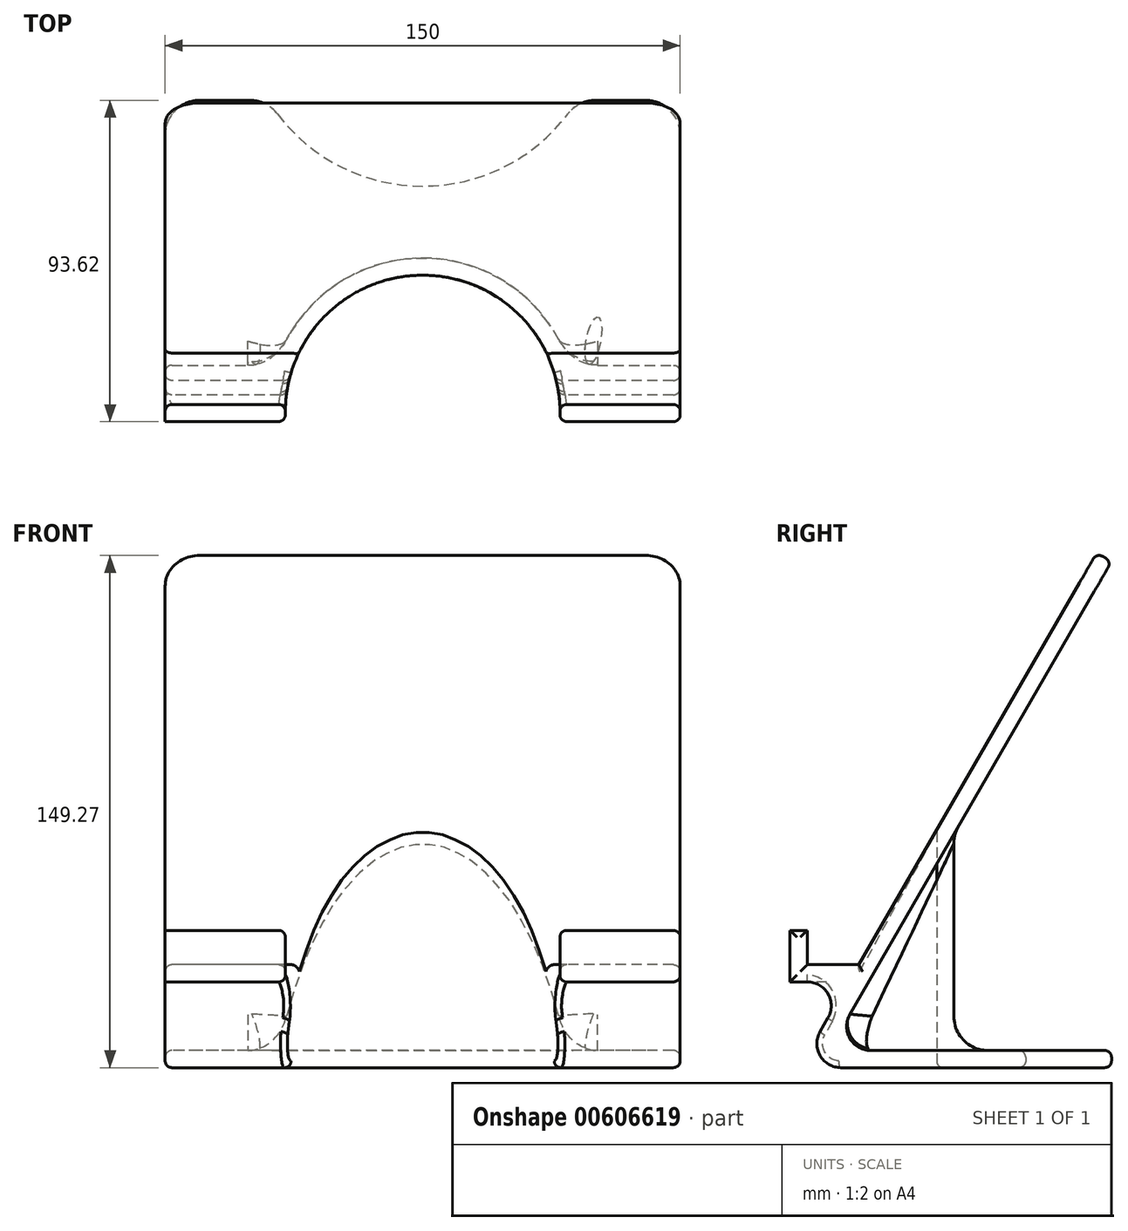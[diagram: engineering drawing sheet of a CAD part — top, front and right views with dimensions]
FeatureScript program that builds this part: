
annotation { "Feature Type Name" : "Feature", "Feature Type Description" : "" }
export const myFeature = defineFeature(function(context is Context, id is Id, definition is map)
    precondition{}
    {
        {
            var Q0;
            Q0=qCreatedBy(makeId("Right.planeOp"),FACE);
            var sketch = newSketch(context, id + "F0", { "sketchPlane" : qUnion([Q0])});
            skLineSegment(sketch, "E0", {"start": v(41.14, -35.62) * mm, "end": v(41.14, -40.62) * mm});
            skLineSegment(sketch, "E1", {"start": v(41.14, -40.62) * mm, "end": v(-49.8, -40.62) * mm});
            skLineSegment(sketch, "E2", {"start": v(-49.8, -40.62) * mm, "end": v(36.8, 109.38) * mm});
            skLineSegment(sketch, "E3", {"start": v(36.8, 109.38) * mm, "end": v(41.14, 106.88) * mm});
            skLineSegment(sketch, "E4", {"start": v(41.14, 106.88) * mm, "end": v(-41.14, -35.62) * mm});
            skLineSegment(sketch, "E5", {"start": v(-41.14, -35.63) * mm, "end": v(41.14, -35.63) * mm});
            skLineSegment(sketch, "E6", {"start": v(0, 35.63) * mm, "end": v(0, -35.63) * mm, "construction": true});
            skSolve(sketch);
        }
        {
            var Q0;
            Q0 = qSketchRegion(id + "F0", true);
            extrude(context, id + "F1", {"entities" : qUnion([Q0]), "endBound" : BoundingType.SYMMETRIC, "depth" : 150 * mm, "offsetDistance" : 25 * mm});
        }
        {
            var Q0;
            Q0=qCreatedBy(makeId("Right.planeOp"),FACE);
            var sketch = newSketch(context, id + "F2", { "sketchPlane" : qUnion([Q0])});
            skLineSegment(sketch, "E7", {"start": v(-29.59, -15.62) * mm, "end": v(-52.48, -15.62) * mm});
            skLineSegment(sketch, "E8", {"start": v(-52.48, -15.62) * mm, "end": v(-52.48, -0.62) * mm});
            skLineSegment(sketch, "E9", {"start": v(-52.48, -0.62) * mm, "end": v(-47.48, -0.62) * mm});
            skLineSegment(sketch, "E10", {"start": v(-47.48, -0.62) * mm, "end": v(-47.48, -10.62) * mm});
            skLineSegment(sketch, "E11", {"start": v(-47.48, -10.62) * mm, "end": v(-29.59, -10.62) * mm});
            skLineSegment(sketch, "E12", {"start": v(-29.59, -10.62) * mm, "end": v(-29.59, -15.62) * mm});
            skPoint(sketch, "E13", {"position": v(-32.48, -10.62) * mm});
            skSolve(sketch);
        }
        {
            var Q0;
            Q0 = qSketchRegion(id + "F2", true);
            var Q1;
            Q1=makeQuery(id+"F1.opExtrude","CAP_FACE",FACE,{"disambiguationData":[OSD([sQuery(id+"F0.wireOp",EDGE,"E0"),sQuery(id+"F0.wireOp",EDGE,"E1"),sQuery(id+"F0.wireOp",EDGE,"E2"),sQuery(id+"F0.wireOp",EDGE,"E3"),sQuery(id+"F0.wireOp",EDGE,"E4"),sQuery(id+"F0.wireOp",EDGE,"E5")])],"isStart":false});
            var Q2;
            Q2=makeQuery(id+"F1.opExtrude","CAP_FACE",FACE,{"disambiguationData":[OSD([sQuery(id+"F0.wireOp",EDGE,"E0"),sQuery(id+"F0.wireOp",EDGE,"E1"),sQuery(id+"F0.wireOp",EDGE,"E2"),sQuery(id+"F0.wireOp",EDGE,"E3"),sQuery(id+"F0.wireOp",EDGE,"E4"),sQuery(id+"F0.wireOp",EDGE,"E5")])],"isStart":true});
            extrude(context, id + "F3", {"entities" : qUnion([Q0]), "operationType" : NewBodyOperationType.ADD, "endBound" : BoundingType.UP_TO_SURFACE, "depth" : 25 * mm, "endBoundEntityFace" : qUnion([Q1]), "offsetDistance" : 25 * mm, "hasSecondDirection" : true, "secondDirectionBound" : SecondDirectionBoundingType.UP_TO_SURFACE, "secondDirectionOppositeDirection" : true, "secondDirectionDepth" : 25 * mm, "secondDirectionBoundEntityFace" : qUnion([Q2])});
        }
        {
            var Q0;
            Q0=makeQuery(id+"F1.opExtrude","SWEPT_FACE",FACE,{"disambiguationData":[OSD([sQuery(id+"F0.wireOp",EDGE,"E1")])]});
            var sketch = newSketch(context, id + "F4", { "sketchPlane" : qUnion([Q0])});
            skCircle(sketch, "E14", {"center": v(0, 49.8) * mm, "radius": 45 * mm});
            skCircle(sketch, "E15", {"center": v(0, 49.8) * mm, "radius": 40 * mm});
            skPoint(sketch, "E16", {"position": v(-45, 49.8) * mm});
            skLineSegment(sketch, "E17.0", {"start": v(75, 49.8) * mm, "end": v(-75, 49.8) * mm});
            skSolve(sketch);
        }
        {
            var Q0;
            {var subQ0=sQuery(id+"F4.wireOp",EDGE,"E17.0");var subQ1=sQuery(id+"F4.wireOp",EDGE,"E14");var subQ2=makeQuery(id+"F4.imprint","INTERSECT",VERTEX,{"disambiguationData":[OD(0.0)],"derivedFrom":[subQ1,subQ0]});Q0=makeQuery(id+"F4.imprint","IMPRINT",FACE,{"disambiguationData":[TD([[makeQuery(id+"F4.imprint","IMPRINT",EDGE,{"disambiguationData":[TD([[subQ2,1.0]])],"derivedFrom":subQ1}),1.0]])]});}
            var Q1;
            Q1=makeQuery(id+"F1.opExtrude","SWEPT_FACE",FACE,{"disambiguationData":[OSD([sQuery(id+"F0.wireOp",EDGE,"E2")])]});
            extrude(context, id + "F5", {"entities" : qUnion([Q0]), "operationType" : NewBodyOperationType.ADD, "endBound" : BoundingType.UP_TO_SURFACE, "oppositeDirection" : true, "depth" : 25 * mm, "endBoundEntityFace" : qUnion([Q1]), "offsetDistance" : 25 * mm});
        }
        {
            var Q0;
            {var subQ0=sQuery(id+"F4.wireOp",EDGE,"E17.0");var subQ1=sQuery(id+"F4.wireOp",EDGE,"E15");var subQ2=makeQuery(id+"F4.imprint","INTERSECT",VERTEX,{"disambiguationData":[OD(0.0)],"derivedFrom":[subQ1,subQ0]});Q0=makeQuery(id+"F4.imprint","IMPRINT",FACE,{"disambiguationData":[TD([[makeQuery(id+"F4.imprint","IMPRINT",EDGE,{"disambiguationData":[TD([[subQ2,1.0]])],"derivedFrom":subQ1}),1.0]])]});}
            var Q1;
            {var subQ0=sQuery(id+"F4.wireOp",EDGE,"E17.0");var subQ1=sQuery(id+"F4.wireOp",EDGE,"E15");var subQ2=makeQuery(id+"F4.imprint","INTERSECT",VERTEX,{"disambiguationData":[OD(0.0)],"derivedFrom":[subQ1,subQ0]});Q1=makeQuery(id+"F4.imprint","IMPRINT",FACE,{"disambiguationData":[TD([[makeQuery(id+"F4.imprint","IMPRINT",EDGE,{"disambiguationData":[TD([[subQ2,-1.0]])],"derivedFrom":subQ1}),1.0]])]});}
            var Q2;
            Q2=makeQuery(id+"F1.opExtrude","SWEPT_FACE",FACE,{"disambiguationData":[OSD([sQuery(id+"F0.wireOp",EDGE,"E2")])]});
            extrude(context, id + "F6", {"entities" : qUnion([Q0, Q1]), "operationType" : NewBodyOperationType.REMOVE, "endBound" : BoundingType.THROUGH_ALL, "oppositeDirection" : true, "depth" : 25 * mm, "endBoundEntityFace" : qUnion([Q2]), "offsetDistance" : 25 * mm});
        }
        {
            var Q0;
            Q0=makeQuery(id+"F1.opExtrude","SWEPT_FACE",FACE,{"disambiguationData":[OSD([sQuery(id+"F0.wireOp",EDGE,"E1")])]});
            var sketch = newSketch(context, id + "F7", { "sketchPlane" : qUnion([Q0])});
            skCircle(sketch, "E18", {"center": v(0, -69.14) * mm, "radius": 53 * mm});
            skPoint(sketch, "E19", {"position": v(-45, -41.14) * mm});
            skPoint(sketch, "E20", {"position": v(0, -16.14) * mm});
            skSolve(sketch);
        }
        {
            var Q0;
            Q0 = qSketchRegion(id + "F7", true);
            var Q1;
            {var subQ0=sQuery(id+"F0.wireOp",EDGE,"E5");var subQ5=sQuery(id+"F0.wireOp",EDGE,"E0");Q1=makeQuery(id+"F5.boolean.opBoolean","SPLIT",FACE,{"disambiguationData":[TD([makeQuery(id+"F1.opExtrude","SWEPT_FACE",FACE,{"disambiguationData":[OSD([subQ5])]})])],"derivedFrom":makeQuery(id+"F1.opExtrude","SWEPT_FACE",FACE,{"disambiguationData":[OSD([subQ0])]})});}
            extrude(context, id + "F8", {"entities" : qUnion([Q0]), "operationType" : NewBodyOperationType.REMOVE, "endBound" : BoundingType.UP_TO_SURFACE, "oppositeDirection" : true, "depth" : 33 * mm, "endBoundEntityFace" : qUnion([Q1]), "offsetDistance" : 25 * mm});
        }
        {
            var Q0;
            {var subQ0=sQuery(id+"F2.wireOp",EDGE,"E7");var subQ1=makeQuery(id+"F3.opExtrude","SWEPT_FACE",FACE,{"disambiguationData":[OSD([subQ0])]});var subQ2=sQuery(id+"F0.wireOp",EDGE,"E2");var subQ3=makeQuery(id+"F1.opExtrude","SWEPT_FACE",FACE,{"disambiguationData":[OSD([subQ2])]});Q0=makeQuery(id+"F6.boolean.opBoolean","SPLIT",EDGE,{"disambiguationData":[TD([makeQuery(id+"F1.opExtrude","CAP_FACE",FACE,{"disambiguationData":[OSD([sQuery(id+"F0.wireOp",EDGE,"E0"),sQuery(id+"F0.wireOp",EDGE,"E1"),subQ2,sQuery(id+"F0.wireOp",EDGE,"E3"),sQuery(id+"F0.wireOp",EDGE,"E4"),sQuery(id+"F0.wireOp",EDGE,"E5")])],"isStart":true})])],"derivedFrom":makeQuery(id+"F3.boolean.opBoolean","INTERSECT",EDGE,{"derivedFrom":[subQ3,subQ1]})});}
            var Q1;
            {var subQ0=sQuery(id+"F2.wireOp",EDGE,"E7");var subQ2=makeQuery(id+"F3.opExtrude","SWEPT_FACE",FACE,{"disambiguationData":[OSD([subQ0])]});var subQ3=sQuery(id+"F0.wireOp",EDGE,"E2");var subQ4=makeQuery(id+"F1.opExtrude","SWEPT_FACE",FACE,{"disambiguationData":[OSD([subQ3])]});Q1=makeQuery(id+"F6.boolean.opBoolean","SPLIT",EDGE,{"disambiguationData":[TD([makeQuery(id+"F1.opExtrude","CAP_FACE",FACE,{"disambiguationData":[OSD([sQuery(id+"F0.wireOp",EDGE,"E0"),sQuery(id+"F0.wireOp",EDGE,"E1"),subQ3,sQuery(id+"F0.wireOp",EDGE,"E3"),sQuery(id+"F0.wireOp",EDGE,"E4"),sQuery(id+"F0.wireOp",EDGE,"E5")])],"isStart":false})])],"derivedFrom":makeQuery(id+"F3.boolean.opBoolean","INTERSECT",EDGE,{"derivedFrom":[subQ4,subQ2]})});}
            var Q2;
            {var subQ0=sQuery(id+"F0.wireOp",EDGE,"E4");var subQ1=sQuery(id+"F0.wireOp",EDGE,"E5");Q2=makeQuery(id+"F5.boolean.opBoolean","SPLIT",EDGE,{"disambiguationData":[TD([makeQuery(id+"F1.opExtrude","CAP_FACE",FACE,{"disambiguationData":[OSD([sQuery(id+"F0.wireOp",EDGE,"E0"),sQuery(id+"F0.wireOp",EDGE,"E1"),sQuery(id+"F0.wireOp",EDGE,"E2"),sQuery(id+"F0.wireOp",EDGE,"E3"),subQ0,subQ1])],"isStart":true})])],"derivedFrom":makeQuery(id+"F1.opExtrude","SWEPT_EDGE",EDGE,{"disambiguationData":[OSD([subQ0,subQ1])]})});}
            var Q3;
            {var subQ0=sQuery(id+"F0.wireOp",EDGE,"E5");var subQ1=sQuery(id+"F0.wireOp",EDGE,"E4");Q3=makeQuery(id+"F5.boolean.opBoolean","SPLIT",EDGE,{"disambiguationData":[TD([makeQuery(id+"F1.opExtrude","CAP_FACE",FACE,{"disambiguationData":[OSD([sQuery(id+"F0.wireOp",EDGE,"E0"),sQuery(id+"F0.wireOp",EDGE,"E1"),sQuery(id+"F0.wireOp",EDGE,"E2"),sQuery(id+"F0.wireOp",EDGE,"E3"),subQ1,subQ0])],"isStart":false})])],"derivedFrom":makeQuery(id+"F1.opExtrude","SWEPT_EDGE",EDGE,{"disambiguationData":[OSD([subQ1,subQ0])]})});}
            var Q4;
            {var subQ0=sQuery(id+"F0.wireOp",EDGE,"E2");var subQ1=sQuery(id+"F0.wireOp",EDGE,"E1");Q4=makeQuery(id+"F6.boolean.opBoolean","SPLIT",EDGE,{"disambiguationData":[TD([makeQuery(id+"F1.opExtrude","CAP_FACE",FACE,{"disambiguationData":[OSD([sQuery(id+"F0.wireOp",EDGE,"E0"),subQ1,subQ0,sQuery(id+"F0.wireOp",EDGE,"E3"),sQuery(id+"F0.wireOp",EDGE,"E4"),sQuery(id+"F0.wireOp",EDGE,"E5")])],"isStart":true})])],"derivedFrom":makeQuery(id+"F1.opExtrude","SWEPT_EDGE",EDGE,{"disambiguationData":[OSD([subQ1,subQ0])]})});}
            var Q5;
            {var subQ1=sQuery(id+"F0.wireOp",EDGE,"E2");var subQ2=sQuery(id+"F0.wireOp",EDGE,"E1");Q5=makeQuery(id+"F6.boolean.opBoolean","SPLIT",EDGE,{"disambiguationData":[TD([makeQuery(id+"F1.opExtrude","CAP_FACE",FACE,{"disambiguationData":[OSD([sQuery(id+"F0.wireOp",EDGE,"E0"),subQ2,subQ1,sQuery(id+"F0.wireOp",EDGE,"E3"),sQuery(id+"F0.wireOp",EDGE,"E4"),sQuery(id+"F0.wireOp",EDGE,"E5")])],"isStart":false})])],"derivedFrom":makeQuery(id+"F1.opExtrude","SWEPT_EDGE",EDGE,{"disambiguationData":[OSD([subQ2,subQ1])]})});}
            fillet(context, id + "F9", {"entities" : qUnion([Q0, Q1, Q2, Q3, Q4, Q5]), "radius" : 7 * mm, "tangentPropagation" : true, "allowEdgeOverflow" : false});
        }
        {
            var Q0;
            Q0=makeQuery(id+"F5.opExtrude","SWEPT_FACE",FACE,{"disambiguationData":[OSD([sQuery(id+"F4.wireOp",EDGE,"E14")])]});
            var Q1;
            Q1=makeQuery(id+"F1.opExtrude","CAP_EDGE",EDGE,{"disambiguationData":[OSD([sQuery(id+"F0.wireOp",EDGE,"E0")])],"isStart":true});
            var Q2;
            Q2=makeQuery(id+"F8.boolean.opBoolean","INTERSECT",EDGE,{"disambiguationData":[OD(0.0)],"derivedFrom":[makeQuery(id+"F1.opExtrude","SWEPT_FACE",FACE,{"disambiguationData":[OSD([sQuery(id+"F0.wireOp",EDGE,"E0")])]}),makeQuery(id+"F8.opExtrude","SWEPT_FACE",FACE,{"disambiguationData":[OSD([sQuery(id+"F7.wireOp",EDGE,"E18")])]})]});
            var Q3;
            Q3=makeQuery(id+"F1.opExtrude","CAP_EDGE",EDGE,{"disambiguationData":[OSD([sQuery(id+"F0.wireOp",EDGE,"E0")])],"isStart":false});
            var Q4;
            Q4=makeQuery(id+"F8.boolean.opBoolean","INTERSECT",EDGE,{"disambiguationData":[OD(1.0)],"derivedFrom":[makeQuery(id+"F1.opExtrude","SWEPT_FACE",FACE,{"disambiguationData":[OSD([sQuery(id+"F0.wireOp",EDGE,"E0")])]}),makeQuery(id+"F8.opExtrude","SWEPT_FACE",FACE,{"disambiguationData":[OSD([sQuery(id+"F7.wireOp",EDGE,"E18")])]})]});
            var Q5;
            Q5=makeQuery(id+"F1.opExtrude","CAP_EDGE",EDGE,{"disambiguationData":[OSD([sQuery(id+"F0.wireOp",EDGE,"E3")])],"isStart":true});
            var Q6;
            Q6=makeQuery(id+"F1.opExtrude","CAP_EDGE",EDGE,{"disambiguationData":[OSD([sQuery(id+"F0.wireOp",EDGE,"E3")])],"isStart":false});
            var Q7;
            {var subQ0=sQuery(id+"F2.wireOp",EDGE,"E8");var subQ1=sQuery(id+"F2.wireOp",EDGE,"E7");Q7=makeQuery(id+"F6.boolean.opBoolean","SPLIT",EDGE,{"disambiguationData":[TD([makeQuery(id+"F1.opExtrude","CAP_FACE",FACE,{"disambiguationData":[OSD([sQuery(id+"F0.wireOp",EDGE,"E0"),sQuery(id+"F0.wireOp",EDGE,"E1"),sQuery(id+"F0.wireOp",EDGE,"E2"),sQuery(id+"F0.wireOp",EDGE,"E3"),sQuery(id+"F0.wireOp",EDGE,"E4"),sQuery(id+"F0.wireOp",EDGE,"E5")])],"isStart":false})])],"derivedFrom":makeQuery(id+"F3.opExtrude","TWEAK_EDGE",EDGE,{"derivedFrom":[makeQuery(id+"F2.imprint","IMPRINT",EDGE,{"derivedFrom":subQ1}),makeQuery(id+"F2.imprint","IMPRINT",EDGE,{"derivedFrom":subQ0})]})});}
            var Q8;
            {var subQ0=sQuery(id+"F2.wireOp",EDGE,"E8");var subQ1=sQuery(id+"F2.wireOp",EDGE,"E7");Q8=makeQuery(id+"F6.boolean.opBoolean","SPLIT",EDGE,{"disambiguationData":[TD([makeQuery(id+"F1.opExtrude","CAP_FACE",FACE,{"disambiguationData":[OSD([sQuery(id+"F0.wireOp",EDGE,"E0"),sQuery(id+"F0.wireOp",EDGE,"E1"),sQuery(id+"F0.wireOp",EDGE,"E2"),sQuery(id+"F0.wireOp",EDGE,"E3"),sQuery(id+"F0.wireOp",EDGE,"E4"),sQuery(id+"F0.wireOp",EDGE,"E5")])],"isStart":true})])],"derivedFrom":makeQuery(id+"F3.opExtrude","TWEAK_EDGE",EDGE,{"derivedFrom":[makeQuery(id+"F2.imprint","IMPRINT",EDGE,{"derivedFrom":subQ1}),makeQuery(id+"F2.imprint","IMPRINT",EDGE,{"derivedFrom":subQ0})]})});}
            fillet(context, id + "F10", {"entities" : qUnion([Q0, Q1, Q2, Q3, Q4, Q5, Q6, Q7, Q8]), "radius" : 10 * mm, "tangentPropagation" : true, "allowEdgeOverflow" : false});
        }
        {
            var Q0;
            Q0=makeQuery(id+"F3.boolean.opBoolean","MERGE",FACE,{"derivedFrom":[makeQuery(id+"F1.opExtrude","CAP_FACE",FACE,{"disambiguationData":[OSD([sQuery(id+"F0.wireOp",EDGE,"E0"),sQuery(id+"F0.wireOp",EDGE,"E1"),sQuery(id+"F0.wireOp",EDGE,"E2"),sQuery(id+"F0.wireOp",EDGE,"E3"),sQuery(id+"F0.wireOp",EDGE,"E4"),sQuery(id+"F0.wireOp",EDGE,"E5")])],"isStart":false}),makeQuery(id+"F3.opExtrude","CAP_FACE",FACE,{"disambiguationData":[OSD([sQuery(id+"F2.wireOp",EDGE,"E7"),sQuery(id+"F2.wireOp",EDGE,"E8"),sQuery(id+"F2.wireOp",EDGE,"E9"),sQuery(id+"F2.wireOp",EDGE,"E10"),sQuery(id+"F2.wireOp",EDGE,"E11"),sQuery(id+"F2.wireOp",EDGE,"E12")])],"isStart":false})]});
            var Q1;
            Q1=makeQuery(id+"F3.opExtrude","CAP_EDGE",EDGE,{"disambiguationData":[OSD([sQuery(id+"F2.wireOp",EDGE,"E10")])],"isStart":true});
            var Q2;
            Q2=makeQuery(id+"F3.opExtrude","CAP_EDGE",EDGE,{"disambiguationData":[OSD([sQuery(id+"F2.wireOp",EDGE,"E11")])],"isStart":true});
            var Q3;
            {var subQ0=sQuery(id+"F4.wireOp",EDGE,"E15");Q3=makeQuery(id+"F6.boolean.opBoolean","MERGE",FACE,{"derivedFrom":[makeQuery(id+"F5.opExtrude","SWEPT_FACE",FACE,{"disambiguationData":[OSD([subQ0])]})],"fromTools":[makeQuery(id+"F6.opExtrude","SWEPT_FACE",FACE,{"disambiguationData":[OSD([subQ0])]})]});}
            fillet(context, id + "F11", {"entities" : qUnion([Q0, Q1, Q2, Q3]), "radius" : 2 * mm, "tangentPropagation" : true, "allowEdgeOverflow" : false});
        }
    });
